# Revit family: RN 92023 Optipress-Aquaplus-Raccordo
name_source: partatom
category: Rohrformteile
units: mm (PartAtom-declared; Revit-internal decimal feet)

## family parameters
Arbeitsebenenbasiert = Nein
Beim Laden mit Abzugskörper schneiden = Nein
Bemaßung runder Anschluss = Durchmesser verwenden
Gemeinsam genutzt = Nein
Immer vertikal = Ja
Teiletyp = Verbindung

## types (7) — shared parameters
1.010.00.2 Blattnummer der Richtlinie = 29
1.010.00.3 Ausgabedatum (Monat) der Richtlinie = 201308
1.010.00.4 Herstellername = R. Nussbaum AG
1.010.00.5 Revisionsdatum der Datei = 20190521
1.010.00.6 Webadresse des Herstellers = http://www.nussbaum.ch
1.100.00.4 Produktbezeichnung = Versorgung
1.110.00.2 Index = 4
1.110.00.4 Produktbezeichnung = Optipress
1.960/3L.00.8 Link (URL) = https://www.nussbaum.ch
29.700.00.4 Produktname = Optipress-A-Anschlussverschraubung, mit Einsteckende
29.700.00.5 Produktkennung = 2
29.700.00.6 Querschnittsform = 1
29.700.00.7 Nennweitensystem = DN
29.700.00.8 Nenndrucksystem = PN
29.710.02.4 Nenndruck = 16
29.710.02.5 max. zul. Überdruck [hPa] = 1600
29.710.02.7 max. zul. Dauer-Betriebsdruck [hPa] = 1600
29.710.02.9 max. zul. Dauer-Betriebstemperatur [°C] = 95
Connector Visibility = Nein
EnclosingSpace Visibility = Nein
Hersteller = R. Nussbaum AG
URL = https://www.nussbaum.ch

## per-type parameters (varying)
| type | 1.800.00.3 TGA-Nummer | 1.800.00.4 Kommentarfeld | 1.810.00.3 Hersteller-Bestellnummer | 1.810.00.4 DATANORM-Nummer | 1.810.00.5 StLB-Nummer | 1.810.00.6 GTIN-Nummer | 29.710.02.10 Formstück-Gewicht [kg] | 29.710.02.3 Benennung | CONNECTOR0_DIAMETER_dX_0r | CONNECTOR0_dX_01 | CONNECTOR0_ref_dX | CONNECTOR1_DIAMETER_dX_0r | CONNECTOR1_dX_00 | CONNECTOR1_dX_01 | CONNECTOR1_ref_dX | Modell | R. Nussbaum AG 92023.22 de Visibility | R. Nussbaum AG 92023.23 de Visibility | R. Nussbaum AG 92023.24 de Visibility | R. Nussbaum AG 92023.25 de Visibility | R. Nussbaum AG 92023.26 de Visibility | R. Nussbaum AG 92023.27 de Visibility | R. Nussbaum AG 92023.28 de Visibility | Typenkommentare |
| DN=50 | 01900400000000000000000000000000000000000000000065000000000000000007 | 92023.28, Optipress-A-Anschlussverschraubung, mit Einsteckende, DN=50, L=55 | 92023.28 | 92023.28 | 671.418 | 7612945037688 | 0.419 | Optipress-A-Anschlussverschraubung, mit Einsteckende, DN=50, L=55 | 50 mm | 40 mm  [stored 0.131234 ft] | 40 mm  [stored 0.131234 ft] | 65 mm | 55 mm | 68 mm | 55 mm | 92023.28 | Nein | Nein | Nein | Nein | Nein | Nein | Ja | Optipress-Aquaplus-Raccordo  DN=50 |
| DN=40 | 01900400000000000000000000000000000000000000000065000000000000000006 | 92023.27, Optipress-A-Anschlussverschraubung, mit Einsteckende, DN=40, L=63 | 92023.27 | 92023.27 | 671.417 | 7612945037671 | 0.269 | Optipress-A-Anschlussverschraubung, mit Einsteckende, DN=40, L=63 | 40 mm  [stored 0.131234 ft] | 36 mm | 36 mm | 50 mm | 64 mm | 75 mm | 64 mm | 92023.27 | Nein | Nein | Nein | Nein | Nein | Ja | Nein | Optipress-Aquaplus-Raccordo  DN=40 |
| DN=32 | 01900400000000000000000000000000000000000000000065000000000000000005 | 92023.26, Optipress-A-Anschlussverschraubung, mit Einsteckende, DN=32, L=46 | 92023.26 | 92023.26 | 671.416 | 7612945037664 | 0.184 | Optipress-A-Anschlussverschraubung, mit Einsteckende, DN=32, L=46 | 32 mm | 26 mm | 26 mm | 40 mm  [stored 0.131234 ft] | 47 mm | 57 mm | 47 mm | 92023.26 | Nein | Nein | Nein | Nein | Ja | Nein | Nein | Optipress-Aquaplus-Raccordo  DN=32 |
| DN=25 | 01900400000000000000000000000000000000000000000065000000000000000004 | 92023.25, Optipress-A-Anschlussverschraubung, mit Einsteckende, DN=25, L=44 | 92023.25 | 92023.25 | 671.415 | 7612945037657 | 0.129 | Optipress-A-Anschlussverschraubung, mit Einsteckende, DN=25, L=44 | 25 mm  [stored 0.082021 ft] | 24 mm | 24 mm | 32 mm | 45 mm | 54 mm | 45 mm | 92023.25 | Nein | Nein | Nein | Ja | Nein | Nein | Nein | Optipress-Aquaplus-Raccordo  DN=25 |
| DN=20 | 01900400000000000000000000000000000000000000000065000000000000000003 | 92023.24, Optipress-A-Anschlussverschraubung, mit Einsteckende, DN=20, L=42 | 92023.24 | 92023.24 | 671.414 | 7612945037640 | 0.082 | Optipress-A-Anschlussverschraubung, mit Einsteckende, DN=20, L=42 | 20 mm | 24 mm | 24 mm | 25 mm  [stored 0.082021 ft] | 42 mm | 51 mm | 42 mm | 92023.24 | Nein | Nein | Ja | Nein | Nein | Nein | Nein | Optipress-Aquaplus-Raccordo  DN=20 |
| DN=15 | 01900400000000000000000000000000000000000000000065000000000000000002 | 92023.23, Optipress-A-Anschlussverschraubung, mit Einsteckende, DN=15, L=41 | 92023.23 | 92023.23 | 671.413 | 7612945037633 | 0.072 | Optipress-A-Anschlussverschraubung, mit Einsteckende, DN=15, L=41 | 15 mm | 22 mm | 22 mm | 20 mm | 41 mm | 49 mm | 41 mm | 92023.23 | Nein | Ja | Nein | Nein | Nein | Nein | Nein | Optipress-Aquaplus-Raccordo  DN=15 |
| DN=12x20 | 01900400000000000000000000000000000000000000000065000000000000000001 | 92023.22, Optipress-A-Anschlussverschraubung, mit Einsteckende, DN=12x20, L=41 | 92023.22 | 92023.22 | 671.412 | 7612945037626 | 0.058 | Optipress-A-Anschlussverschraubung, mit Einsteckende, DN=12x20, L=41 | 12 mm  [stored 0.0393701 ft] | 22 mm | 22 mm | 20 mm | 41 mm | 49 mm | 41 mm | 92023.22 | Ja | Nein | Nein | Nein | Nein | Nein | Nein | Optipress-Aquaplus-Raccordo  DN=12x20 |

note: [stored X ft] marks values corroborated as IEEE doubles in the binary element streams (Revit-internal decimal feet)

## geometry (parser evidence)
native form markers: Sweep x1
no freeform markers — native parametric forms only
